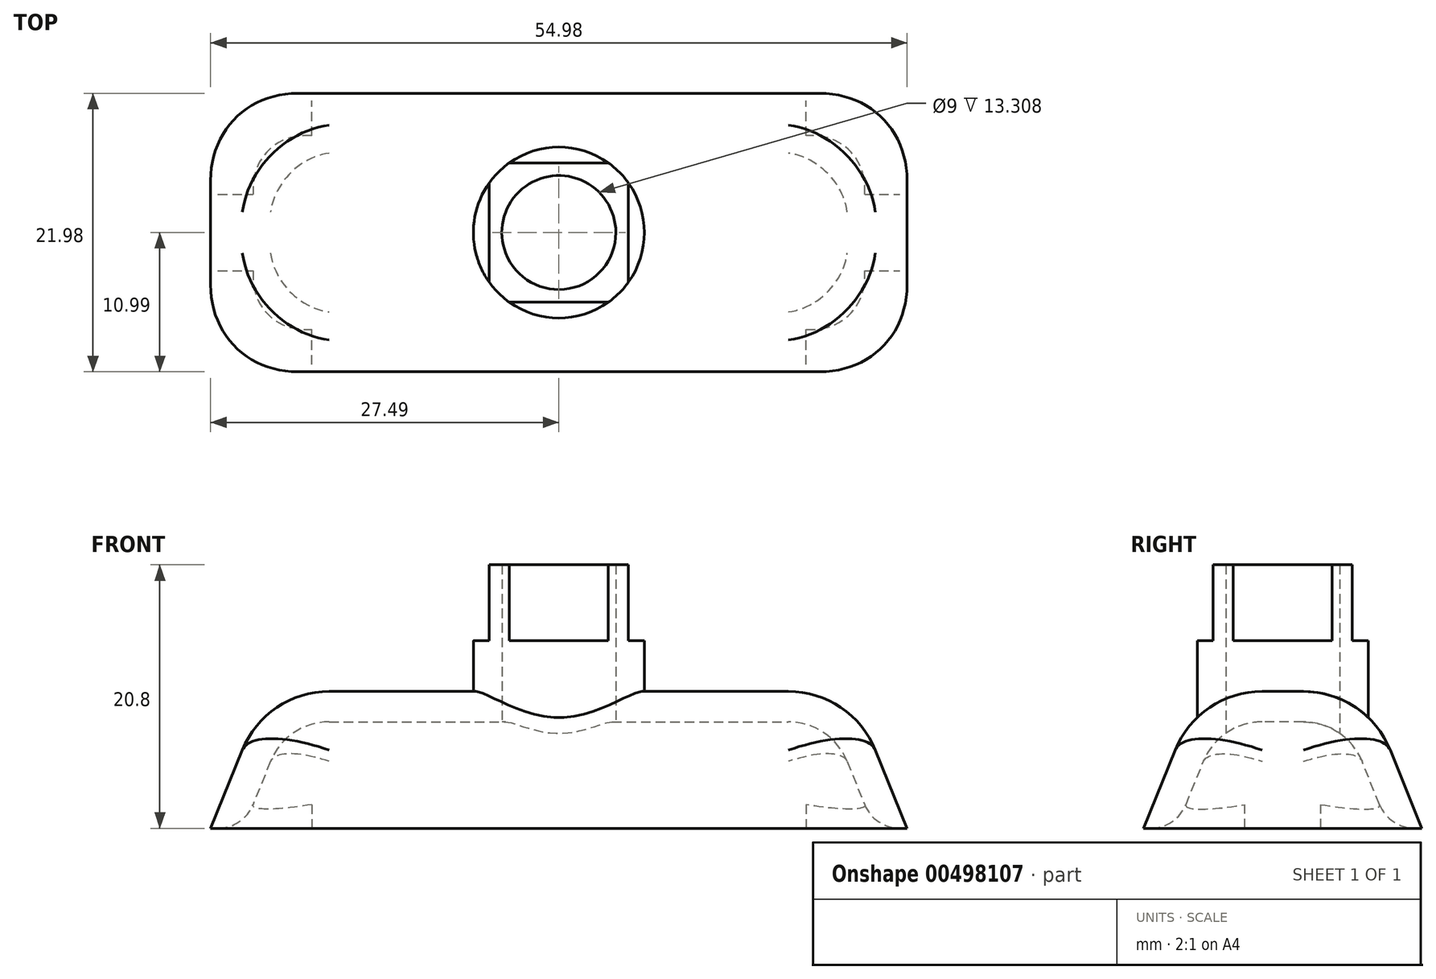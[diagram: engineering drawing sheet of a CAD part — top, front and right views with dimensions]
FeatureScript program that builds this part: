
annotation { "Feature Type Name" : "Feature", "Feature Type Description" : "" }
export const myFeature = defineFeature(function(context is Context, id is Id, definition is map)
    precondition{}
    {
        {
            var Q0;
            Q0=qCreatedBy(makeId("Front.planeOp"),FACE);
            var sketch = newSketch(context, id + "F0", { "sketchPlane" : qUnion([Q0])});
            skLineSegment(sketch, "E0.bottom", {"start": v(24.9, -4.2) * mm, "end": v(-24.9, -4.2) * mm});
            skLineSegment(sketch, "E0.top", {"start": v(24.9, 4.2) * mm, "end": v(-24.9, 4.2) * mm});
            skLineSegment(sketch, "E0.left", {"start": v(24.9, -4.2) * mm, "end": v(24.9, 4.2) * mm});
            skLineSegment(sketch, "E0.right", {"start": v(-24.9, -4.2) * mm, "end": v(-24.9, 4.2) * mm});
            skPoint(sketch, "E0.middle", {"position": v(0, 0) * mm});
            skSolve(sketch);
        }
        {
            var Q0;
            Q0 = qSketchRegion(id + "F0", true);
            extrude(context, id + "F1", {"entities" : qUnion([Q0]), "endBound" : BoundingType.SYMMETRIC, "depth" : 16.8 * mm});
        }
        {
            var Q0;
            Q0=makeQuery(id+"F1.opExtrude","CAP_EDGE",EDGE,{"disambiguationData":[OSD([sQuery(id+"F0.wireOp",EDGE,"E0.top")])],"isStart":false});
            var Q1;
            Q1=makeQuery(id+"F1.opExtrude","SWEPT_EDGE",EDGE,{"disambiguationData":[OSD([sQuery(id+"F0.wireOp",EDGE,"E0.top"),sQuery(id+"F0.wireOp",EDGE,"E0.right")])]});
            var Q2;
            Q2=makeQuery(id+"F1.opExtrude","CAP_EDGE",EDGE,{"disambiguationData":[OSD([sQuery(id+"F0.wireOp",EDGE,"E0.top")])],"isStart":true});
            var Q3;
            Q3=makeQuery(id+"F1.opExtrude","SWEPT_EDGE",EDGE,{"disambiguationData":[OSD([sQuery(id+"F0.wireOp",EDGE,"E0.top"),sQuery(id+"F0.wireOp",EDGE,"E0.left")])]});
            chamfer(context, id + "F2", {"entities" : qUnion([Q0, Q1, Q2, Q3]), "chamferType" : ChamferType.TWO_OFFSETS, "width1" : 8.4 * mm, "oppositeDirection" : false, "width2" : 3.4 * mm, "tangentPropagation" : true});
        }
        {
            var Q0;
            {var subQ0=sQuery(id+"F0.wireOp",EDGE,"E0.top");Q0=makeQuery(id+"F2.opChamfer","BLEND_EDGE",EDGE,{"blendedFrom":[makeQuery(id+"F1.opExtrude","SWEPT_EDGE",EDGE,{"disambiguationData":[OSD([subQ0,sQuery(id+"F0.wireOp",EDGE,"E0.right")])]}),makeQuery(id+"F1.opExtrude","CAP_EDGE",EDGE,{"disambiguationData":[OSD([subQ0])],"isStart":false})],"blendedInto":[]});}
            var Q1;
            {var subQ0=sQuery(id+"F0.wireOp",EDGE,"E0.top");Q1=makeQuery(id+"F2.opChamfer","BLEND_EDGE",EDGE,{"blendedFrom":[makeQuery(id+"F1.opExtrude","SWEPT_EDGE",EDGE,{"disambiguationData":[OSD([subQ0,sQuery(id+"F0.wireOp",EDGE,"E0.left")])]}),makeQuery(id+"F1.opExtrude","CAP_EDGE",EDGE,{"disambiguationData":[OSD([subQ0])],"isStart":false})],"blendedInto":[]});}
            var Q2;
            {var subQ0=sQuery(id+"F0.wireOp",EDGE,"E0.top");Q2=makeQuery(id+"F2.opChamfer","BLEND_EDGE",EDGE,{"blendedFrom":[makeQuery(id+"F1.opExtrude","SWEPT_EDGE",EDGE,{"disambiguationData":[OSD([subQ0,sQuery(id+"F0.wireOp",EDGE,"E0.left")])]}),makeQuery(id+"F1.opExtrude","CAP_EDGE",EDGE,{"disambiguationData":[OSD([subQ0])],"isStart":true})],"blendedInto":[]});}
            var Q3;
            {var subQ0=sQuery(id+"F0.wireOp",EDGE,"E0.top");Q3=makeQuery(id+"F2.opChamfer","BLEND_EDGE",EDGE,{"blendedFrom":[makeQuery(id+"F1.opExtrude","SWEPT_EDGE",EDGE,{"disambiguationData":[OSD([subQ0,sQuery(id+"F0.wireOp",EDGE,"E0.right")])]}),makeQuery(id+"F1.opExtrude","CAP_EDGE",EDGE,{"disambiguationData":[OSD([subQ0])],"isStart":true})],"blendedInto":[]});}
            var Q4;
            {var subQ0=sQuery(id+"F0.wireOp",EDGE,"E0.top");Q4=makeQuery(id+"F2.opChamfer","BLEND_EDGE",EDGE,{"blendedFrom":[makeQuery(id+"F1.opExtrude","CAP_EDGE",EDGE,{"disambiguationData":[OSD([subQ0])],"isStart":false}),makeQuery(id+"F1.opExtrude","SWEPT_FACE",FACE,{"disambiguationData":[OSD([subQ0])]})],"blendedInto":[makeQuery(id+"F1.opExtrude","SWEPT_FACE",FACE,{"disambiguationData":[OSD([subQ0])]})]});}
            var Q5;
            {var subQ0=sQuery(id+"F0.wireOp",EDGE,"E0.top");Q5=makeQuery(id+"F2.opChamfer","BLEND_EDGE",EDGE,{"blendedFrom":[makeQuery(id+"F1.opExtrude","CAP_EDGE",EDGE,{"disambiguationData":[OSD([subQ0])],"isStart":true}),makeQuery(id+"F1.opExtrude","SWEPT_FACE",FACE,{"disambiguationData":[OSD([subQ0])]})],"blendedInto":[makeQuery(id+"F1.opExtrude","SWEPT_FACE",FACE,{"disambiguationData":[OSD([subQ0])]})]});}
            var Q6;
            {var subQ0=sQuery(id+"F0.wireOp",EDGE,"E0.top");Q6=makeQuery(id+"F2.opChamfer","BLEND_EDGE",EDGE,{"blendedFrom":[makeQuery(id+"F1.opExtrude","SWEPT_EDGE",EDGE,{"disambiguationData":[OSD([subQ0,sQuery(id+"F0.wireOp",EDGE,"E0.left")])]}),makeQuery(id+"F1.opExtrude","SWEPT_FACE",FACE,{"disambiguationData":[OSD([subQ0])]})],"blendedInto":[makeQuery(id+"F1.opExtrude","SWEPT_FACE",FACE,{"disambiguationData":[OSD([subQ0])]})]});}
            var Q7;
            {var subQ0=sQuery(id+"F0.wireOp",EDGE,"E0.top");Q7=makeQuery(id+"F2.opChamfer","BLEND_EDGE",EDGE,{"blendedFrom":[makeQuery(id+"F1.opExtrude","SWEPT_EDGE",EDGE,{"disambiguationData":[OSD([subQ0,sQuery(id+"F0.wireOp",EDGE,"E0.right")])]}),makeQuery(id+"F1.opExtrude","SWEPT_FACE",FACE,{"disambiguationData":[OSD([subQ0])]})],"blendedInto":[makeQuery(id+"F1.opExtrude","SWEPT_FACE",FACE,{"disambiguationData":[OSD([subQ0])]})]});}
            fillet(context, id + "F3", {"entities" : qUnion([Q0, Q1, Q2, Q3, Q4, Q5, Q6, Q7]), "radius" : 5 * mm, "tangentPropagation" : true, "allowEdgeOverflow" : false});
        }
        {
            var Q0;
            Q0=makeQuery(id+"F1.opExtrude","SWEPT_FACE",FACE,{"disambiguationData":[OSD([sQuery(id+"F0.wireOp",EDGE,"E0.bottom")])]});
            shell(context, id + "F4", {"entities" : qUnion([Q0]), "thickness" : 2.4 * mm, "oppositeDirection" : true});
        }
        {
            var Q0;
            Q0=makeQuery(id+"F1.opExtrude","SWEPT_FACE",FACE,{"disambiguationData":[OSD([sQuery(id+"F0.wireOp",EDGE,"E0.top")])]});
            var sketch = newSketch(context, id + "F5", { "sketchPlane" : qUnion([Q0])});
            skCircle(sketch, "E1", {"center": v(0, 0) * mm, "radius": 6.75 * mm});
            skSolve(sketch);
        }
        {
            var Q0;
            Q0 = qSketchRegion(id + "F5", true);
            var Q1;
            Q1=sQuery(id+"F5.wireOp",EDGE,"E1");
            extrude(context, id + "F6", {"entities" : qUnion([Q0]), "operationType" : NewBodyOperationType.ADD, "surfaceEntities" : qUnion([Q1]), "depth" : 10 * mm, "hasSecondDirection" : true, "secondDirectionOppositeDirection" : true, "secondDirectionDepth" : 2.2 * mm});
        }
        {
            var Q0;
            Q0=qCreatedBy(makeId("Top.planeOp"),FACE);
            var sketch = newSketch(context, id + "F7", { "sketchPlane" : qUnion([Q0])});
            skCircle(sketch, "E2", {"center": v(0, 0) * mm, "radius": 4.5 * mm});
            skSolve(sketch);
        }
        {
            var Q0;
            Q0 = qSketchRegion(id + "F7", true);
            var Q1;
            Q1=sQuery(id+"F7.wireOp",EDGE,"E2");
            extrude(context, id + "F8", {"entities" : qUnion([Q0]), "operationType" : NewBodyOperationType.REMOVE, "surfaceEntities" : qUnion([Q1]), "endBound" : BoundingType.THROUGH_ALL, "depth" : 25 * mm});
        }
        {
            var Q0;
            Q0=makeQuery(id+"F6.opExtrude","CAP_FACE",FACE,{"disambiguationData":[OSD([sQuery(id+"F5.wireOp",EDGE,"E1")])],"isStart":false});
            var sketch = newSketch(context, id + "F9", { "sketchPlane" : qUnion([Q0])});
            skCircle(sketch, "E3.0", {"center": v(0, 0) * mm, "radius": 6.75 * mm});
            skLineSegment(sketch, "E4.bottom", {"start": v(3.91, 5.5) * mm, "end": v(-3.91, 5.5) * mm});
            skLineSegment(sketch, "E4.top", {"start": v(3.91, -5.5) * mm, "end": v(-3.91, -5.5) * mm});
            skLineSegment(sketch, "E4.left", {"start": v(5.5, 3.91) * mm, "end": v(5.5, -3.91) * mm});
            skLineSegment(sketch, "E4.right", {"start": v(-5.5, 3.91) * mm, "end": v(-5.5, -3.91) * mm});
            skPoint(sketch, "E5", {"position": v(-3.91, 5.5) * mm});
            skPoint(sketch, "E6", {"position": v(3.91, 5.5) * mm});
            skPoint(sketch, "E7", {"position": v(5.5, 3.91) * mm});
            skPoint(sketch, "E8", {"position": v(5.5, -3.91) * mm});
            skPoint(sketch, "E9", {"position": v(3.91, -5.5) * mm});
            skPoint(sketch, "E10", {"position": v(-3.91, -5.5) * mm});
            skPoint(sketch, "E11", {"position": v(-5.5, -3.91) * mm});
            skPoint(sketch, "E12", {"position": v(-5.5, 3.91) * mm});
            skPoint(sketch, "E13.orphan", {"position": v(-5.5, 5.5) * mm});
            skPoint(sketch, "E14.orphan", {"position": v(5.5, 5.5) * mm});
            skPoint(sketch, "E15.orphan", {"position": v(5.5, -5.5) * mm});
            skPoint(sketch, "E16.orphan", {"position": v(-5.5, -5.5) * mm});
            skSolve(sketch);
        }
        {
            var Q0;
            {var subQ0=sQuery(id+"F9.wireOp",EDGE,"E4.left");Q0=makeQuery(id+"F9.imprint","IMPRINT",FACE,{"disambiguationData":[TD([[makeQuery(id+"F9.imprint","IMPRINT",EDGE,{"derivedFrom":subQ0}),1.0]])]});}
            var Q1;
            {var subQ0=sQuery(id+"F9.wireOp",EDGE,"E4.top");Q1=makeQuery(id+"F9.imprint","IMPRINT",FACE,{"disambiguationData":[TD([[makeQuery(id+"F9.imprint","IMPRINT",EDGE,{"derivedFrom":subQ0}),1.0]])]});}
            var Q2;
            {var subQ0=sQuery(id+"F9.wireOp",EDGE,"E4.right");Q2=makeQuery(id+"F9.imprint","IMPRINT",FACE,{"disambiguationData":[TD([[makeQuery(id+"F9.imprint","IMPRINT",EDGE,{"derivedFrom":subQ0}),-1.0]])]});}
            var Q3;
            {var subQ0=sQuery(id+"F9.wireOp",EDGE,"E4.bottom");Q3=makeQuery(id+"F9.imprint","IMPRINT",FACE,{"disambiguationData":[TD([[makeQuery(id+"F9.imprint","IMPRINT",EDGE,{"derivedFrom":subQ0}),-1.0]])]});}
            extrude(context, id + "F10", {"entities" : qUnion([Q0, Q1, Q2, Q3]), "operationType" : NewBodyOperationType.REMOVE, "oppositeDirection" : true, "depth" : 6 * mm});
        }
        {
            var Q0;
            {var subQ0=sQuery(id+"F0.wireOp",EDGE,"E0.bottom");var subQ1=sQuery(id+"F0.wireOp",EDGE,"E0.top");Q0=makeQuery(id+"F4.opShell","OFFSET_EDGE",EDGE,{"disambiguationData":[OSD([subQ0,subQ1]),TDD([makeQuery(id+"F2.opChamfer","BLEND_EDGE",EDGE,{"blendedFrom":[makeQuery(id+"F1.opExtrude","CAP_EDGE",EDGE,{"disambiguationData":[OSD([subQ1])],"isStart":false}),makeQuery(id+"F1.opExtrude","SWEPT_FACE",FACE,{"disambiguationData":[OSD([subQ0])]})],"blendedInto":[makeQuery(id+"F1.opExtrude","SWEPT_FACE",FACE,{"disambiguationData":[OSD([subQ0])]})]})])]});}
            fillet(context, id + "F11", {"entities" : qUnion([Q0]), "radius" : 3 * mm, "tangentPropagation" : true, "allowEdgeOverflow" : false});
        }
    });
